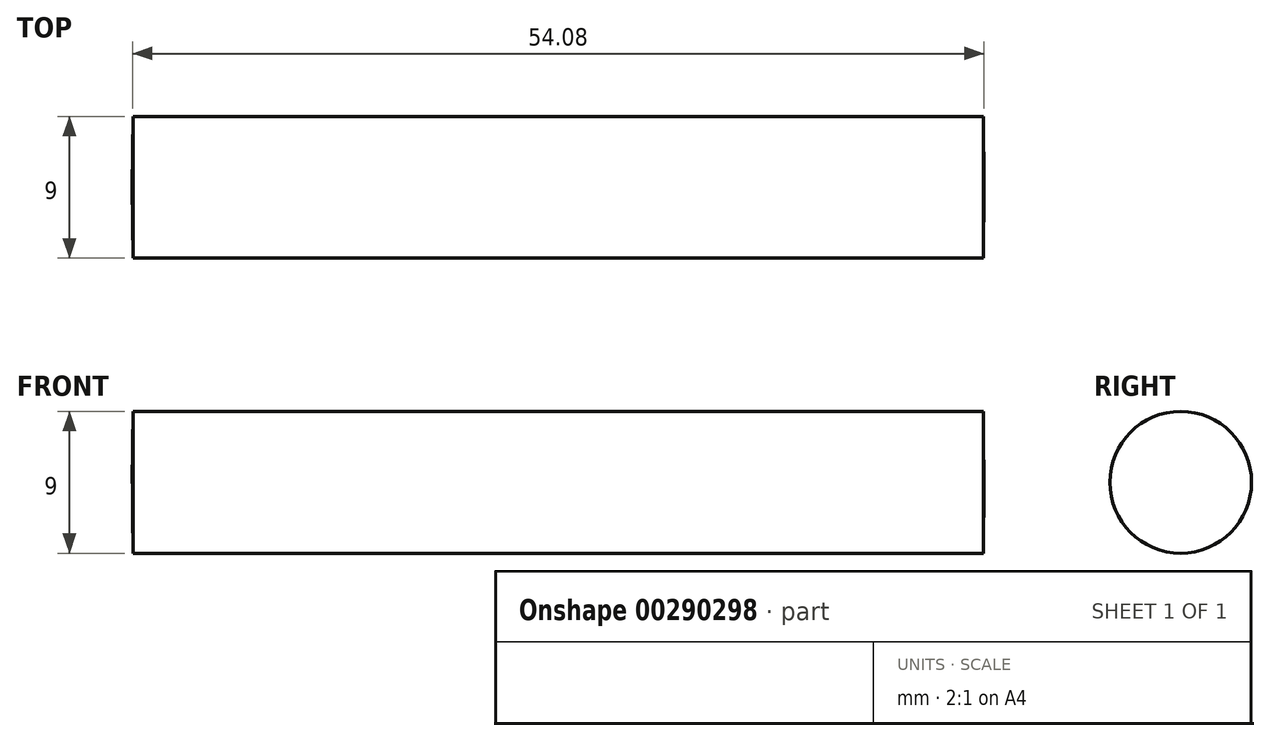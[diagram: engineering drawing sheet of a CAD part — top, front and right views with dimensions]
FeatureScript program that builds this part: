
annotation { "Feature Type Name" : "Feature", "Feature Type Description" : "" }
export const myFeature = defineFeature(function(context is Context, id is Id, definition is map)
    precondition{}
    {
        {
            var Q0;
            Q0=qCreatedBy(makeId("Front.planeOp"),FACE);
            var sketch = newSketch(context, id + "F0", { "sketchPlane" : qUnion([Q0])});
            skLineSegment(sketch, "E0", {"start": v(0, 4.5) * mm, "end": v(27, 4.5) * mm});
            skLineSegment(sketch, "E1.MirrorCS", {"start": v(0, 4.5) * mm, "end": v(-27, 4.5) * mm});
            skLineSegment(sketch, "E2", {"start": v(-27.04, 0) * mm, "end": v(27.04, 0) * mm});
            skLineSegment(sketch, "E3", {"start": v(-27, 4.5) * mm, "end": v(-27.04, 0) * mm});
            skLineSegment(sketch, "E4", {"start": v(27, 4.5) * mm, "end": v(27.04, 0) * mm});
            skSolve(sketch);
        }
        {
            var Q0;
            Q0=makeQuery(id+"F0.imprint","IMPRINT",FACE,{"disambiguationData":[TD([[makeQuery(id+"F0.imprint","IMPRINT",EDGE,{"derivedFrom":sQuery(id+"F0.wireOp",EDGE,"E0")}),-1.0]])]});
            var Q1;
            Q1=sQuery(id+"F0.wireOp",EDGE,"E2");
            revolve(context, id + "F1", {"entities" : qUnion([Q0]), "axis" : qUnion([Q1]), "revolveType" : RevolveType.FULL});
        }
    });
